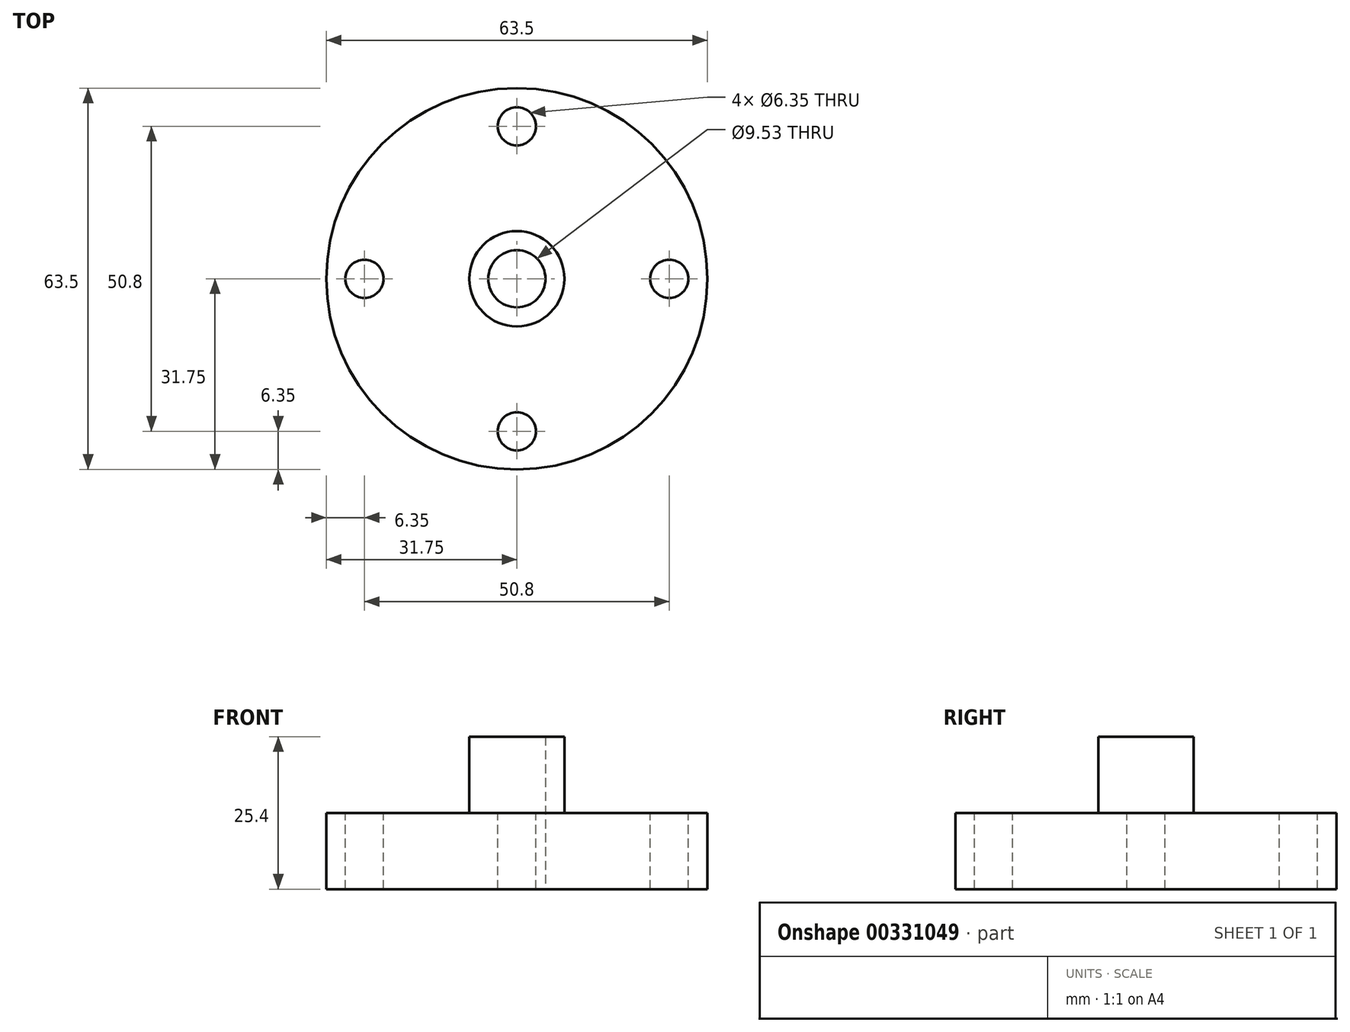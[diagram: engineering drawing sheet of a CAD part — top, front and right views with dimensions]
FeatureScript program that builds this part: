
annotation { "Feature Type Name" : "Feature", "Feature Type Description" : "" }
export const myFeature = defineFeature(function(context is Context, id is Id, definition is map)
    precondition{}
    {
        {
            var Q0;
            Q0=qCreatedBy(makeId("Top.planeOp"),FACE);
            var sketch = newSketch(context, id + "F0", { "sketchPlane" : qUnion([Q0])});
            skCircle(sketch, "E0", {"center": v(0, 0) * mm, "radius": 31.75 * mm});
            skSolve(sketch);
        }
        {
            var Q0;
            Q0 = qSketchRegion(id + "F0", true);
            extrude(context, id + "F1", {"entities" : qUnion([Q0]), "oppositeDirection" : true, "depth" : 12.7 * mm});
        }
        {
            var Q0;
            Q0=makeQuery(id+"F1.opExtrude","CAP_FACE",FACE,{"disambiguationData":[OSD([sQuery(id+"F0.wireOp",EDGE,"E0")])],"isStart":true});
            var sketch = newSketch(context, id + "F2", { "sketchPlane" : qUnion([Q0])});
            skCircle(sketch, "E1", {"center": v(0, 0) * mm, "radius": 7.94 * mm});
            skCircle(sketch, "E2", {"center": v(0, 0) * mm, "radius": 4.76 * mm});
            skSolve(sketch);
        }
        {
            var Q0;
            Q0 = qSketchRegion(id + "F2", true);
            extrude(context, id + "F3", {"entities" : qUnion([Q0]), "operationType" : NewBodyOperationType.ADD, "depth" : 12.7 * mm});
        }
        {
            var Q0;
            Q0=makeQuery(id+"F3.boolean.opBoolean","SPLIT",FACE,{"disambiguationData":[TD([makeQuery(id+"F3.opExtrude","SWEPT_FACE",FACE,{"disambiguationData":[OSD([sQuery(id+"F2.wireOp",EDGE,"E2")])]})])],"derivedFrom":makeQuery(id+"F1.opExtrude","CAP_FACE",FACE,{"disambiguationData":[OSD([sQuery(id+"F0.wireOp",EDGE,"E0")])],"isStart":true})});
            extrude(context, id + "F4", {"entities" : qUnion([Q0]), "operationType" : NewBodyOperationType.REMOVE, "oppositeDirection" : true, "depth" : 25.4 * mm});
        }
        {
            var Q0;
            {var subQ0=sQuery(id+"F0.wireOp",EDGE,"E0");Q0=makeQuery(id+"F3.boolean.opBoolean","SPLIT",FACE,{"disambiguationData":[TD([makeQuery(id+"F1.opExtrude","SWEPT_FACE",FACE,{"disambiguationData":[OSD([subQ0])]})])],"derivedFrom":makeQuery(id+"F1.opExtrude","CAP_FACE",FACE,{"disambiguationData":[OSD([subQ0])],"isStart":true})});}
            var sketch = newSketch(context, id + "F5", { "sketchPlane" : qUnion([Q0])});
            skCircle(sketch, "E3", {"center": v(-25.4, 0) * mm, "radius": 3.18 * mm});
            skCircle(sketch, "E4.1.0", {"center": v(0, -25.4) * mm, "radius": 3.18 * mm});
            skCircle(sketch, "E4.2.0", {"center": v(25.4, 0) * mm, "radius": 3.18 * mm});
            skCircle(sketch, "E4.3.0", {"center": v(0, 25.4) * mm, "radius": 3.18 * mm});
            skPoint(sketch, "E4.center", {"position": v(0, 0) * mm});
            skSolve(sketch);
        }
        {
            var Q0;
            Q0 = qSketchRegion(id + "F5", true);
            extrude(context, id + "F6", {"entities" : qUnion([Q0]), "operationType" : NewBodyOperationType.REMOVE, "oppositeDirection" : true, "depth" : 25.4 * mm});
        }
    });
